FCSTD DOCUMENT  (FreeCAD 0.21R33694 (Git))
Label: MiniITXModular
License: All rights reserved
LicenseURL: http://en.wikipedia.org/wiki/All_rights_reserved
objects: Sketcher::SketchObject×4, Spreadsheet::Sheet×1, PartDesign::Plane×1, PartDesign::Body×1
note: 6 computed .brp shape members not serialized (recipe doc carries the construction recipe); baked Part::Feature solids carry a one-line shape summary decoded from their .brp

FEATURE [Spreadsheet::Sheet] Spreadsheet
  cells = B2='Tolerance; C2(Tolerance)==0.1 mm; B3='WallTolerance; C3(WallTolerance)==0.2 mm; B4='PrintLineWidth; C4(PrintLineWidth)==0.4 mm; B5='GuideWidth; C5(GuideWidth)==8 mm; B6='WallInset; C6(WallInset)==0.8 mm; B7='WallThickness; C7(WallThickness)==1.6 mm; B8='WallDriveDepth; C8(WallDriveDepth)==1 mm
FEATURE [Sketcher::SketchObject] Sketch001  label="Front"
  FullyConstrained = true
  MapMode = 5
  Placement = pos=(0,0,0) rot=(1,0,0;1.5708rad)
  Support = -> [XZ_Plane]
  expr: Constraints[79] = <<Spreadsheet>>.WallThickness
  expr: Constraints[92] = <<Spreadsheet>>.WallThickness + <<Spreadsheet>>.WallTolerance
  sketch-geometry (39):
    g0: LineSegment StartX=5.40261 StartY=54.7987 StartZ=0 EndX=44.1357 EndY=54.7987 EndZ=0
    g1: LineSegment StartX=44.1357 StartY=54.7987 StartZ=0 EndX=50.4026 EndY=48.5318 EndZ=0
    g2: LineSegment StartX=50.4026 StartY=48.5318 StartZ=0 EndX=50.4026 EndY=11.0656 EndZ=0
    g3: LineSegment StartX=50.4026 StartY=11.0656 StartZ=0 EndX=44.1357 EndY=4.79874 EndZ=0
    g4: LineSegment StartX=44.1357 StartY=4.79874 StartZ=0 EndX=5.40261 EndY=4.79874 EndZ=0
    g5: LineSegment StartX=5.40261 StartY=4.79874 StartZ=0 EndX=7.52393 EndY=6.92006 EndZ=0
    g6: LineSegment StartX=7.52393 StartY=6.92006 StartZ=0 EndX=7.52393 EndY=9.46564 EndZ=0
    g7: LineSegment StartX=7.52393 StartY=9.46564 StartZ=0 EndX=5.40261 EndY=7.34432 EndZ=0
    g8: LineSegment StartX=5.40261 StartY=7.34432 StartZ=0 EndX=5.40261 EndY=9.60706 EndZ=0
    g9: LineSegment StartX=5.40261 StartY=9.60706 StartZ=0 EndX=7.52393 EndY=11.7284 EndZ=0
    g10: LineSegment StartX=7.52393 StartY=11.7284 StartZ=0 EndX=9.52393 EndY=11.7284 EndZ=0
    g11: LineSegment StartX=14.8536 StartY=6.39874 StartZ=0 EndX=43.473 EndY=6.39874 EndZ=0
    g12: LineSegment StartX=43.473 StartY=6.39874 StartZ=0 EndX=48.8026 EndY=11.7284 EndZ=0
    g13: LineSegment StartX=48.8026 StartY=11.7284 StartZ=0 EndX=48.8026 EndY=47.8691 EndZ=0
    g14: LineSegment StartX=48.8026 StartY=47.8691 StartZ=0 EndX=43.473 EndY=53.1987 EndZ=0
    g15: LineSegment StartX=43.473 StartY=53.1987 StartZ=0 EndX=14.8536 EndY=53.1987 EndZ=0
    g16: LineSegment StartX=9.52393 StartY=47.8691 StartZ=0 EndX=7.52393 EndY=47.8691 EndZ=0
    g17: LineSegment StartX=7.52393 StartY=47.8691 StartZ=0 EndX=5.40261 EndY=49.9904 EndZ=0
    g18: LineSegment StartX=5.40261 StartY=49.9904 StartZ=0 EndX=5.40261 EndY=52.2532 EndZ=0
    g19: LineSegment StartX=5.40261 StartY=52.2532 StartZ=0 EndX=7.52393 EndY=50.1318 EndZ=0
    g20: LineSegment StartX=7.52393 StartY=50.1318 StartZ=0 EndX=7.52393 EndY=52.6774 EndZ=0
    g21: LineSegment StartX=7.52393 StartY=52.6774 StartZ=0 EndX=5.40261 EndY=54.7987 EndZ=0
    g22: LineSegment StartX=5.40261 StartY=49.9904 StartZ=0 EndX=5.40261 EndY=9.60706 EndZ=0
    g23: LineSegment StartX=5.40261 StartY=7.34432 StartZ=0 EndX=5.40261 EndY=4.79874 EndZ=0
    g24: LineSegment StartX=5.40261 StartY=52.2532 StartZ=0 EndX=5.40261 EndY=54.7987 EndZ=0
    g25: LineSegment StartX=7.52393 StartY=50.1318 StartZ=0 EndX=7.52393 EndY=47.8691 EndZ=0
    g26: LineSegment StartX=7.52393 StartY=9.46564 StartZ=0 EndX=7.52393 EndY=11.7284 EndZ=0
    g27: LineSegment StartX=9.52393 StartY=47.8691 StartZ=0 EndX=9.52393 EndY=11.7284 EndZ=0
    g28: LineSegment StartX=43.473 StartY=53.1987 StartZ=0 EndX=44.6043 EndY=54.3301 EndZ=0
    g29: LineSegment StartX=48.8026 StartY=11.7284 StartZ=0 EndX=49.934 EndY=10.597 EndZ=0
    g30: LineSegment StartX=14.8536 StartY=6.39874 StartZ=0 EndX=14.8536 EndY=4.79874 EndZ=0
    g31: LineSegment StartX=14.8536 StartY=53.1987 StartZ=0 EndX=14.8536 EndY=54.7987 EndZ=0
    g32: LineSegment StartX=48.8026 StartY=47.8691 StartZ=0 EndX=50.4026 EndY=47.8691 EndZ=0
    g33: LineSegment StartX=43.473 StartY=6.39874 StartZ=0 EndX=43.473 EndY=53.1987 EndZ=0
    g34: LineSegment StartX=5.40261 StartY=49.9904 StartZ=0 EndX=6.53398 EndY=51.1218 EndZ=0
    g35: LineSegment StartX=9.52393 StartY=47.8691 StartZ=0 EndX=14.8536 EndY=53.1987 EndZ=0
    g36: LineSegment StartX=5.40261 StartY=52.2532 StartZ=0 EndX=6.67541 EndY=53.5259 EndZ=0
    g37: LineSegment StartX=9.52393 StartY=11.7284 StartZ=0 EndX=14.8536 EndY=6.39874 EndZ=0
    g38: LineSegment StartX=14.8536 StartY=53.1987 StartZ=0 EndX=14.8536 EndY=6.39874 EndZ=0
  constraints (110):
    c: Horizontal(g0)
    c: Coincident(g0,g1)
    c: Coincident(g1,g2)
    c: Vertical(g2)
    c: Coincident(g2,g3)
    c: Coincident(g3,g4)
    c: Horizontal(g4)
    c: Coincident(g4,g5)
    c: Coincident(g5,g6)
    c: Vertical(g6)
    c: Coincident(g6,g7)
    c: Coincident(g7,g8)
    c: Vertical(g8)
    c: Coincident(g8,g9)
    c: Coincident(g9,g10)
    c: Horizontal(g11)
    c: Coincident(g11,g12)
    c: Coincident(g12,g13)
    c: Vertical(g13)
    c: Coincident(g13,g14)
    c: Coincident(g14,g15)
    c: Horizontal(g15)
    c: Coincident(g16,g17)
    c: Coincident(g17,g18)
    c: Vertical(g18)
    c: Coincident(g18,g19)
    c: Coincident(g19,g20)
    c: Vertical(g20)
    c: Coincident(g20,g21)
    c: Coincident(g22,g17)
    c: Coincident(g22,g8)
    c: Vertical(g22)
    c: Coincident(g23,g7)
    c: Coincident(g23,g4)
    c: Vertical(g23)
    c: Coincident(g24,g18)
    c: Coincident(g24,g21)
    c: Vertical(g24)
    c: Coincident(g0,g21)
    c: Coincident(g25,g19)
    c: Coincident(g25,g16)
    c: Vertical(g25)
    c: Coincident(g26,g6)
    c: Coincident(g9,g26)
    c: Vertical(g26)
    c: Equal(g23,g6)
    c: Equal(g8,g26)
    c: Horizontal(g10)
    c: Equal(g24,g20)
    c: Equal(g25,g18)
    c: Horizontal(g16)
    c: Coincident(g27,g10)
    c: Vertical(g27)
    c: Equal(g10,g16)
    c: Equal(g8,g18)
    c: Parallel(g1,g14)
    c: Parallel(g12,g3)
    c: Coincident(g28,g14)
    c: PointOnObject(g28,g1)
    c: Coincident(g29,g12)
    c: PointOnObject(g29,g3)
    c: PointOnObject(g30,g4)
    c: Vertical(g30)
    c: PointOnObject(g31,g0)
    c: Vertical(g31)
    c: Coincident(g32,g13)
    c: PointOnObject(g32,g2)
    c: Equal(g30,g29)
    c: Equal(g29,g32)
    c: Equal(g32,g28)
    c: Equal(g28,g31)
    c: Angle(g12,g11) = 2.35619
    c: Coincident(g33,g11)
    c: Coincident(g33,g14)
    c: Vertical(g33)
    c: Equal(g12,g14)
    c: Perpendicular(g1,g28)
    c: Horizontal(g32)
    c: Perpendicular(g3,g29)
    c: DistanceX(g13,g1) = 1.6
    c: DistanceX(g16,g16) = 2
    c: Coincident(g34,g17)
    c: PointOnObject(g34,g19)
    c: Perpendicular(g19,g34)
    c: Equal(g31,g34)
    c: Angle(g18,g19) = 0.785398
    c: Coincident(g15,g31)
    c: Coincident(g35,g15)
    c: Perpendicular(g21,g35)
    c: Coincident(g36,g18)
    c: PointOnObject(g36,g21)
    c: Perpendicular(g21,g36)
    c: Distance(g36) = 1.8
    c: Distance(g21) = 3
    c: Equal(g5,g21)
    c: Coincident(g11,g30)
    c: Coincident(g37,g11)
    c: Coincident(g38,g15)
    c: Coincident(g38,g11)
    c: Vertical(g38)
    c: Equal(g35,g37)
    c: DistanceY(g11,g10) = 5.32965
    c: DistanceX(g0,g1) = 45
    c: PointOnObject(g13,g16)
    c: DistanceY(g3,g0) = 50
    c: DistanceX(g4) = 5.40261
    c: DistanceY(g4) = 4.79874
    c: Coincident(g16,g27)
    c: Coincident(g16,g35)
    c: Coincident(g37,g10)
FEATURE [Sketcher::SketchObject] Sketch  label="Motherboard_top"
  FullyConstrained = true
  MapMode = 5
  Support = -> [XY_Plane]
  sketch-geometry (16):
    g0: LineSegment StartX=-85.09 StartY=85.09 StartZ=0 EndX=85.09 EndY=85.09 EndZ=0
    g1: LineSegment StartX=85.09 StartY=85.09 StartZ=0 EndX=85.09 EndY=-85.09 EndZ=0
    g2: LineSegment StartX=85.09 StartY=-85.09 StartZ=0 EndX=-85.09 EndY=-85.09 EndZ=0
    g3: LineSegment StartX=-85.09 StartY=-85.09 StartZ=0 EndX=-85.09 EndY=85.09 EndZ=0
    g4: Circle CenterX=-78.74 CenterY=74.93 CenterZ=0 NormalX=0 NormalY=0 NormalZ=1 AngleXU=0 Radius=2.032
    g5: Circle CenterX=78.74 CenterY=52.07 CenterZ=0 NormalX=0 NormalY=0 NormalZ=1 AngleXU=0 Radius=2.032
    g6: Circle CenterX=78.74 CenterY=-80.01 CenterZ=0 NormalX=0 NormalY=0 NormalZ=1 AngleXU=0 Radius=2.032
    g7: Circle CenterX=-78.74 CenterY=-80.01 CenterZ=0 NormalX=0 NormalY=0 NormalZ=1 AngleXU=0 Radius=2.032
    g8: LineSegment StartX=-78.74 StartY=74.93 StartZ=0 EndX=-78.74 EndY=-80.01 EndZ=0
    g9: LineSegment StartX=-78.74 StartY=-80.01 StartZ=0 EndX=78.74 EndY=-80.01 EndZ=0
    g10: LineSegment StartX=78.74 StartY=-80.01 StartZ=0 EndX=78.74 EndY=52.07 EndZ=0
    g11: LineSegment StartX=-71.12 StartY=85.09 StartZ=0 EndX=-71.12 EndY=87.59 EndZ=0
    g12: LineSegment StartX=87.63 StartY=87.59 StartZ=0 EndX=87.63 EndY=85.09 EndZ=0
    g13: LineSegment StartX=85.09 StartY=85.09 StartZ=0 EndX=87.63 EndY=85.09 EndZ=0
    g14: LineSegment StartX=-71.12 StartY=87.59 StartZ=0 EndX=87.63 EndY=87.59 EndZ=0
    g15: LineSegment StartX=3e-16 StartY=87.59 StartZ=0 EndX=3e-16 EndY=-85.09 EndZ=0
  constraints (46):
    c: Coincident(g0,g1)
    c: Coincident(g1,g2)
    c: Coincident(g2,g3)
    c: Coincident(g3,g0)
    c: Horizontal(g0)
    c: Horizontal(g2)
    c: Vertical(g1)
    c: Vertical(g3)
    c: Equal(g0,g3)
    c: DistanceX(g0,g0) = 170.18  'Width'
    c: Equal(g4,g5)
    c: Equal(g5,g6)
    c: Equal(g6,g7)
    c: Radius(g7) = 2.032
    c: Symmetric(g2,g0,g-1)
    c: Coincident(g8,g4)
    c: Vertical(g8)
    c: DistanceY(g4,g0) = 10.16
    c: DistanceX(g0,g4) = 6.35
    c: Coincident(g7,g8)
    c: DistanceY(g7,g4) = 154.94
    c: Coincident(g9,g7)
    c: Coincident(g9,g6)
    c: Horizontal(g9)
    c: Coincident(g10,g6)
    c: Coincident(g10,g5)
    c: Vertical(g10)
    c: DistanceY(g5,g4) = 22.86
    c: DistanceX(g9,g9) = 157.48
    c: PointOnObject(g11,g0)
    c: Vertical(g11)
    c: Vertical(g12)
    c: DistanceX(g4,g11) = 7.62
    c: DistanceX(g11,g12) = 158.75
    c: Coincident(g13,g0)
    c: Coincident(g13,g12)
    c: Horizontal(g13)
    c: Horizontal(g14)
    c: DistanceY(g12,g14) = 2.5  'ShieldOffset'
    c: DistanceY(g5,g0) = 33.02
    c: Coincident(g11,g14)
    c: Coincident(g12,g14)
    c: DistanceX(g0,g12) = 2.54  'ShieldShootout'
    c: PointOnObject(g15,g2)
    c: PointOnObject(g15,g14)
    c: Symmetric(g0,g0,g15)
FEATURE [Sketcher::SketchObject] Sketch002  label="PSU_top"
  FullyConstrained = true
  MapMode = 5
  Support = -> [XY_Plane]
  sketch-geometry (12):
    g0: LineSegment StartX=-77 StartY=15 StartZ=0 EndX=77 EndY=15 EndZ=0
    g1: LineSegment StartX=77 StartY=15 StartZ=0 EndX=77 EndY=4 EndZ=0
    g2: LineSegment StartX=77 StartY=-15 StartZ=0 EndX=-77 EndY=-15 EndZ=0
    g3: LineSegment StartX=-77 StartY=-15 StartZ=0 EndX=-77 EndY=0 EndZ=0
    g4: LineSegment StartX=-77 StartY=4 StartZ=0 EndX=-71.6 EndY=4 EndZ=0
    g5: LineSegment StartX=-77 StartY=0 StartZ=0 EndX=-71.6 EndY=0 EndZ=0
    g6: LineSegment StartX=77 StartY=4 StartZ=0 EndX=67.6 EndY=4 EndZ=0
    g7: LineSegment StartX=77 StartY=4e-16 StartZ=0 EndX=67.6 EndY=4e-16 EndZ=0
    g8: ArcOfCircle CenterX=-71.6 CenterY=2 CenterZ=0 NormalX=0 NormalY=0 NormalZ=1 AngleXU=0 Radius=2 StartAngle=4.71239 EndAngle=7.85398
    g9: ArcOfCircle CenterX=67.6 CenterY=2 CenterZ=0 NormalX=0 NormalY=0 NormalZ=1 AngleXU=0 Radius=2 StartAngle=1.5708 EndAngle=4.71239
    g10: LineSegment StartX=77 StartY=4e-16 StartZ=0 EndX=77 EndY=-15 EndZ=0
    g11: LineSegment StartX=-77 StartY=4 StartZ=0 EndX=-77 EndY=15 EndZ=0
  constraints (34):
    c: Coincident(g0,g1)
    c: Coincident(g10,g2)
    c: Coincident(g2,g3)
    c: Coincident(g11,g0)
    c: Horizontal(g0)
    c: Horizontal(g2)
    c: Vertical(g1)
    c: Vertical(g3)
    c: Symmetric(g2,g0,g-1)
    c: DistanceX(g0,g0) = 154
    c: DistanceY(g3,g11) = 30
    c: Horizontal(g5)
    c: Horizontal(g6)
    c: Horizontal(g7)
    c: Horizontal(g4)
    c: PointOnObject(g6,g4)
    c: DistanceY(g4,g0) = 11
    c: DistanceY(g2,g5) = 15
    c: PointOnObject(g7,g5)
    c: Radius(g8) = 2
    c: DistanceX(g0,g4) = 5.4
    c: DistanceX(g6,g0) = 9.4
    c: Tangent(g9,g7) = 1.5708
    c: Tangent(g9,g6) = -1.5708
    c: Tangent(g8,g4) = 1.5708
    c: Tangent(g8,g5) = -1.5708
    c: Coincident(g1,g6)
    c: Coincident(g10,g7)
    c: Coincident(g3,g5)
    c: Coincident(g11,g4)
    c: PointOnObject(g3,g11)
    c: Vertical(g11)
    c: Vertical(g10)
    c: PointOnObject(g7,g1)
FEATURE [PartDesign::Plane] DatumPlane
  Length = 171.55
  MapMode = 7
  Placement = pos=(3e-16,87.59,0) rot=(0,0.707107,0.707107;3.14159rad)
  ResizeMode = 0
  Support = -> [Sketch]
  Width = 67.5499
FEATURE [Sketcher::SketchObject] Sketch003
  ExternalGeometry = -> [Sketch]
  FullyConstrained = true
  MapMode = 5
  Placement = pos=(3e-16,87.59,0) rot=(0,0.707107,0.707107;3.14159rad)
  Support = -> [DatumPlane]
FEATURE [PartDesign::Body] Body  label="Templates"
  Group = -> [Sketch001,Sketch,Sketch002,DatumPlane,Sketch003]
  Origin = -> Origin
